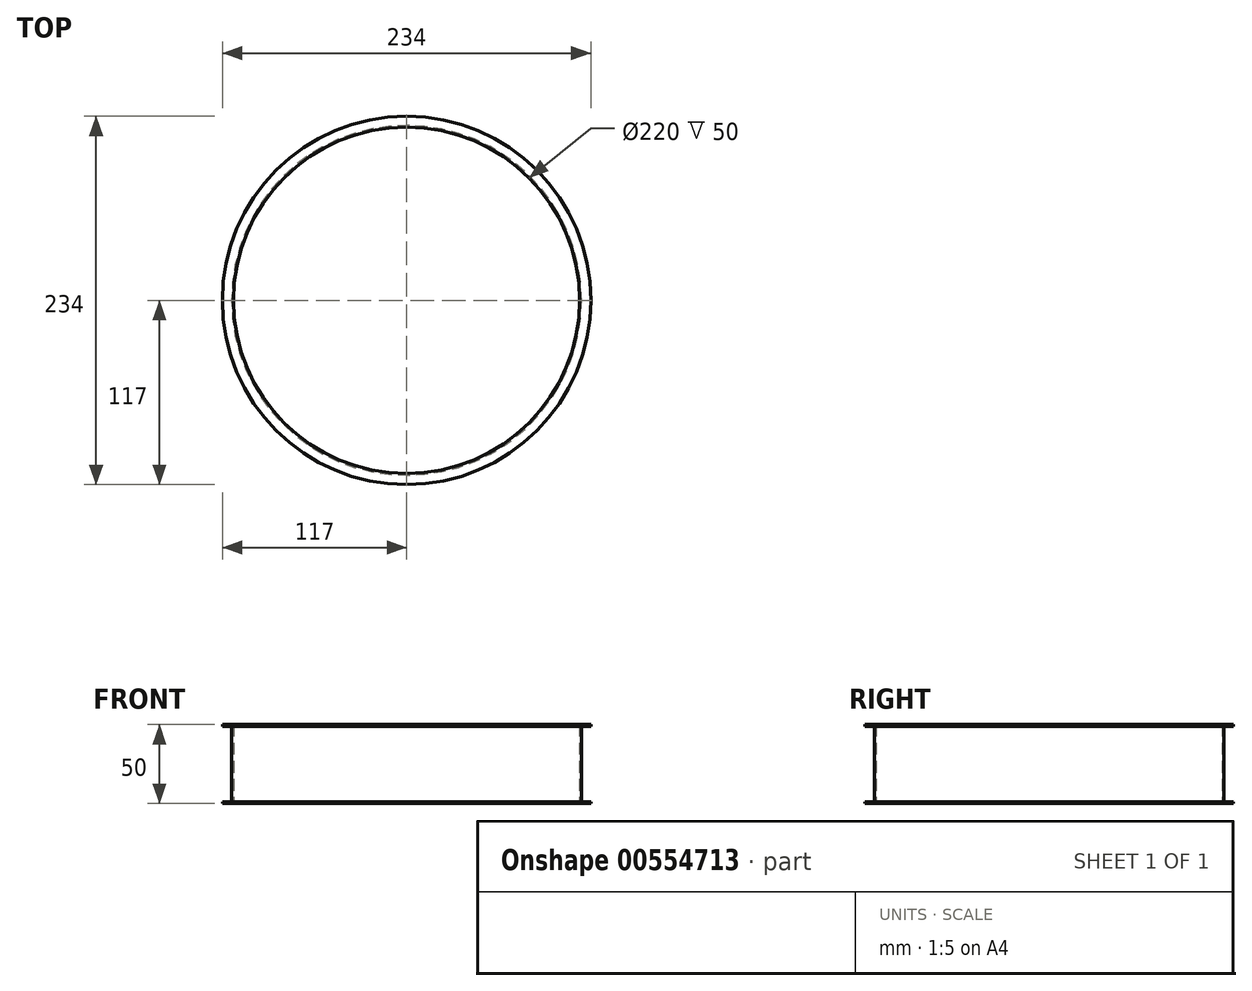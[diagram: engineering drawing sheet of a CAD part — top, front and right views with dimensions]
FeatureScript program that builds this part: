
annotation { "Feature Type Name" : "Feature", "Feature Type Description" : "" }
export const myFeature = defineFeature(function(context is Context, id is Id, definition is map)
    precondition{}
    {
        {
            var Q0;
            Q0=qCreatedBy(makeId("Front.planeOp"),FACE);
            var sketch = newSketch(context, id + "F0", { "sketchPlane" : qUnion([Q0])});
            skLineSegment(sketch, "E0.bottom", {"start": v(0, 0) * mm, "end": v(-110, 0) * mm});
            skLineSegment(sketch, "E0.top", {"start": v(0, 25) * mm, "end": v(-110, 25) * mm});
            skLineSegment(sketch, "E0.left", {"start": v(0, 0) * mm, "end": v(0, 25) * mm});
            skLineSegment(sketch, "E0.right", {"start": v(-110, 0) * mm, "end": v(-110, 25) * mm});
            skLineSegment(sketch, "E1", {"start": v(-110, 0) * mm, "end": v(-111, 0) * mm});
            skLineSegment(sketch, "E2", {"start": v(-111, 0) * mm, "end": v(-111, 24) * mm});
            skLineSegment(sketch, "E3", {"start": v(-111, 24) * mm, "end": v(-117, 24) * mm});
            skLineSegment(sketch, "E4", {"start": v(-117, 24) * mm, "end": v(-117, 25) * mm});
            skLineSegment(sketch, "E5", {"start": v(-117, 25) * mm, "end": v(-110, 25) * mm});
            skLineSegment(sketch, "E6.MirrorCS", {"start": v(-117, -24) * mm, "end": v(-117, -25) * mm});
            skLineSegment(sketch, "E7.MirrorCS", {"start": v(-111, -24) * mm, "end": v(-117, -24) * mm});
            skLineSegment(sketch, "E8.MirrorCS", {"start": v(-111, 0) * mm, "end": v(-111, -24) * mm});
            skLineSegment(sketch, "E9.MirrorCS", {"start": v(-110, 0) * mm, "end": v(-110, -25) * mm});
            skLineSegment(sketch, "E10.MirrorCS", {"start": v(-117, -25) * mm, "end": v(-110, -25) * mm});
            skSolve(sketch);
        }
        {
            var Q0;
            Q0=makeQuery(id+"F0.imprint","IMPRINT",FACE,{"disambiguationData":[TD([[makeQuery(id+"F0.imprint","IMPRINT",EDGE,{"derivedFrom":sQuery(id+"F0.wireOp",EDGE,"E0.right")}),1.0]])]});
            var Q1;
            Q1=makeQuery(id+"F0.imprint","IMPRINT",FACE,{"disambiguationData":[TD([[makeQuery(id+"F0.imprint","IMPRINT",EDGE,{"derivedFrom":sQuery(id+"F0.wireOp",EDGE,"E1")}),1.0]])]});
            var Q2;
            Q2=sQuery(id+"F0.wireOp",EDGE,"E0.left");
            revolve(context, id + "F1", {"entities" : qUnion([Q0, Q1]), "axis" : qUnion([Q2]), "revolveType" : RevolveType.FULL});
        }
    });
